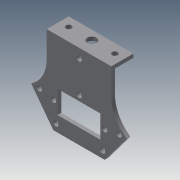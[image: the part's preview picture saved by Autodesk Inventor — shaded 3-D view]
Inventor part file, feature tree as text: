
AUTODESK INVENTOR PART (.ipt)
format: ipt  version: 2015 (Build 190159000, 159)  size: 1,127,936 bytes
history: native  units: mm
features: sketch x103, extrude x90, fillet x2
ambient origin geometry x8: Origin, YZ Plane, XZ Plane, XY Plane, X Axis, Y Axis, Z Axis, Center Point
bodies: Solid1 (feature_tree)
feature tree (195):
  extrude  "Extrusion1"  Depth=10.0mm
  extrude  "Extrusion2"  Depth=10.0mm
  sketch  "Sketch3"  dims[d8=2.0mm d9=0.0mm d11=3.0mm]
  extrude  "Extrusion3"  Depth=2.0mm
  extrude  "Extrusion4"  Depth=3.0mm
  extrude  "Extrusion5"  Depth=10.0mm TaperAngle=0.0deg
  extrude  "Extrusion6"  Depth=3.0mm
  sketch  "Sketch8"  dims[d24=10.0mm d25=0.0mm d26=2.0mm d27=0.0mm]
  extrude  "Extrusion7"  Depth=3.0mm
  extrude  "Extrusion8"  Depth=2.0mm TaperAngle=0.0deg
  extrude  "Extrusion9"  Depth=3.0mm
  extrude  "Extrusion10"  Depth=2.0mm TaperAngle=0.0deg
  extrude  "Extrusion11"  Depth=2.0mm
  extrude  "Extrusion12"  Depth=12.0mm
  extrude  "Extrusion13"  Depth=2.0mm
  sketch  "Sketch16"  dims[d61=4.0mm d62=4.0mm]
  extrude  "Extrusion14"  Depth=2.0mm
  extrude  "Extrusion15"  Depth=12.0mm
  extrude  "Extrusion16"  Depth=4.0mm
  extrude  "Extrusion17"  Depth=2.0mm
  sketch  "Sketch21"  dims[d75=30.0mm d77=2.0mm d78=0.0mm]
  extrude  "Extrusion18"  Depth=12.0mm
  extrude  "Extrusion19"  Depth=2.0mm
  extrude  "Extrusion20"  Depth=20.0mm
  extrude  "Extrusion21"  Depth=2.0mm TaperAngle=0.0deg
  extrude  "Extrusion22"  Depth=2.3mm
  extrude  "Extrusion23"  Depth=2.0mm
  extrude  "Extrusion24"  Depth=2.0mm TaperAngle=0.0deg
  extrude  "Extrusion25"  Depth=3.0mm
  extrude  "Extrusion26"  Depth=2.0mm TaperAngle=0.0deg
  extrude  "Extrusion27"  Depth=2.0mm TaperAngle=0.0deg
  extrude  "Extrusion28"  Depth=4.0mm
  extrude  "Extrusion29"  Depth=3.0mm
  extrude  "Extrusion30"  Depth=3.0mm
  extrude  "Extrusion31"  Depth=3.0mm
  extrude  "Extrusion32"  Depth=4.0mm
  extrude  "Extrusion33"  Depth=3.0mm
  extrude  "Extrusion34"  Depth=2.0mm TaperAngle=0.0deg
  extrude  "Extrusion35"  Depth=2.3mm
  extrude  "Extrusion36"  Depth=4.0mm
  extrude  "Extrusion37"  Depth=2.0mm
  sketch  "Sketch42"  dims[d147=24.0mm d148=24.0mm]
  sketch  "Sketch43"  dims[d149=2.0mm d150=0.0mm d151=2.0mm d152=0.0mm]
  extrude  "Extrusion38"  Depth=2.0mm TaperAngle=0.0deg
  extrude  "Extrusion39"  Depth=2.0mm TaperAngle=0.0deg
  extrude  "Extrusion40"  Depth=20.0mm
  extrude  "Extrusion41"  Depth=20.0mm
  extrude  "Extrusion42"  Depth=24.0mm
  extrude  "Extrusion43"  Depth=2.0mm TaperAngle=0.0deg
  extrude  "Extrusion44"  Depth=3.0mm
  extrude  "Extrusion45"  Depth=20.0mm
  extrude  "Extrusion46"  Depth=2.0mm TaperAngle=0.0deg
  extrude  "Extrusion47"  Depth=2.0mm
  extrude  "Extrusion48"  Depth=3.0mm
  fillet  "Fillet1"  Radius=3.0mm
  extrude  "Extrusion49"  Depth=2.5mm
  fillet  "Fillet2"  Radius=2.0mm
  extrude  "Extrusion50"  Depth=2.0mm
  extrude  "Extrusion51"  Depth=2.5mm
  extrude  "Extrusion52"  Depth=20.0mm
  extrude  "Extrusion53"  Depth=20.0mm
  extrude  "Extrusion54"  Depth=2.0mm TaperAngle=0.0deg
  extrude  "Extrusion55"  Depth=1.5mm
  extrude  "Extrusion56"  Depth=20.0mm
  extrude  "Extrusion57"  Depth=20.0mm
  extrude  "Extrusion58"  Depth=24.0mm
  extrude  "Extrusion59"  Depth=2.0mm
  extrude  "Extrusion60"  Depth=3.0mm
  extrude  "Extrusion61"  Depth=3.0mm
  extrude  "Extrusion62"  Depth=2.0mm TaperAngle=0.0deg
  sketch  "Sketch67"  dims[d218=3.0mm d219=3.0mm]
  extrude  "Extrusion63"  Depth=2.0mm
  extrude  "Extrusion64"  Depth=2.0mm TaperAngle=0.0deg
  extrude  "Extrusion65"  Depth=14.4mm
  sketch  "Sketch71"  dims[d228=1.5mm d229=3.0mm]
  sketch  "Sketch72"  dims[d230=2.0mm d231=0.0mm d233=2.0mm d234=0.0mm]
  extrude  "Extrusion66"  Depth=1.5mm
  sketch  "Sketch73"  dims[d236=14.5mm d237=13.95mm]
  sketch  "Sketch74"  dims[d238=13.95mm d239=3.0mm]
  extrude  "Extrusion67"  Depth=3.0mm
  extrude  "Extrusion68"  Depth=2.0mm TaperAngle=0.0deg
  extrude  "Extrusion69"  Depth=1.5mm
  extrude  "Extrusion70"  Depth=14.4mm
  extrude  "Extrusion71"  Depth=1.5mm
  sketch  "Sketch80"  dims[d256=19.0mm d259=19.0mm]
  sketch  "Sketch81"  dims[d260=2.0mm d261=0.0mm d262=10.0mm]
  extrude  "Extrusion72"  Depth=2.0mm TaperAngle=0.0deg
  extrude  "Extrusion73"  Depth=13.95mm
  sketch  "Sketch84"  dims[d269=2.0mm d270=0.0mm d271=2.0mm d272=0.0mm]
  extrude  "Extrusion74"  Depth=3.0mm
  extrude  "Extrusion75"  Depth=2.0mm TaperAngle=0.0deg
  extrude  "Extrusion76"  Depth=2.0mm
  extrude  "Extrusion77"  Depth=2.0mm
  extrude  "Extrusion78"  Depth=2.0mm
  extrude  "Extrusion79"  Depth=2.0mm TaperAngle=0.0deg
  extrude  "Extrusion80"  Depth=19.0mm
  extrude  "Extrusion81"  Depth=10.0mm
  extrude  "Extrusion82"  Depth=4.0mm
  extrude  "Extrusion83"  Depth=2.0mm TaperAngle=0.0deg
  sketch  "Sketch95"  dims[d298=10.0mm d299=0.0mm]
  extrude  "Extrusion84"  Depth=2.0mm TaperAngle=0.0deg
  extrude  "Extrusion85"  Depth=2.0mm TaperAngle=0.0deg
  extrude  "Extrusion86"  Depth=10.0mm TaperAngle=0.0deg
  extrude  "Extrusion87"  Depth=2.0mm TaperAngle=0.0deg
  sketch  "Sketch100"  dims[d310=16.0mm]
  extrude  "Extrusion88"  Depth=1.5mm TaperAngle=0.0deg
  extrude  "Extrusion89"  Depth=1.5mm
  extrude  "Extrusion90"  Depth=16.0mm
  sketch  "Sketch1"  dims[d2=10.0mm d3=10.0mm]
  sketch  "Sketch2"  dims[d4=10.0mm d7=10.0mm]
  sketch  "Sketch4"  dims[d12=3.0mm d14=3.0mm]
  sketch  "Sketch5"  dims[d15=3.0mm d16=10.0mm d17=0.0mm]
  sketch  "Sketch6"  dims[d20=6.0mm d21=3.0mm]
  sketch  "Sketch7"  dims[d22=6.0mm d23=3.0mm]
  sketch  "Sketch9"  dims[d34=3.0mm d36=3.0mm]
  sketch  "Sketch10"  dims[d37=2.0mm d38=0.0mm d39=2.0mm d40=0.0mm]
  sketch  "Sketch11"  dims[d48=2.0mm d49=4.0mm]
  sketch  "Sketch12"  dims[d51=12.0mm d52=4.0mm]
  sketch  "Sketch13"  dims[d53=2.0mm d54=0.0mm d55=1.8mm]
  sketch  "Sketch14"  dims[d56=2.0mm d57=4.0mm]
  sketch  "Sketch15"  dims[d58=2.0mm d59=0.0mm d60=12.0mm]
  sketch  "Sketch17"  dims[d63=2.0mm d64=0.0mm d65=16.0mm]
  sketch  "Sketch18"  dims[d66=12.0mm d67=10.4mm]
  sketch  "Sketch19"  dims[d68=2.0mm d69=0.0mm d70=4.0mm]
  sketch  "Sketch20"  dims[d71=2.0mm d72=0.0mm d74=20.0mm]
  sketch  "Sketch22"  dims[d83=2.3mm d84=2.3mm]
  sketch  "Sketch23"  dims[d85=2.0mm d86=0.0mm d90=24.0mm]
  sketch  "Sketch24"  dims[d92=24.0mm d93=2.0mm d94=0.0mm]
  sketch  "Sketch25"  dims[d97=3.0mm d98=3.0mm]
  sketch  "Sketch26"  dims[d100=3.0mm d101=2.0mm d102=0.0mm]
  sketch  "Sketch27"  dims[d103=2.0mm d104=0.0mm d105=2.0mm d106=0.0mm]
  sketch  "Sketch28"  dims[d111=4.0mm d112=4.0mm]
  sketch  "Sketch29"  dims[d113=3.0mm d114=3.0mm]
  sketch  "Sketch30"  dims[d116=3.0mm d117=3.0mm]
  sketch  "Sketch31"  dims[d118=3.0mm d119=3.0mm]
  sketch  "Sketch32"  dims[d120=3.0mm d121=4.0mm]
  sketch  "Sketch33"  dims[d122=3.0mm d123=3.0mm]
  sketch  "Sketch34"  dims[d124=3.0mm d125=2.0mm d126=0.0mm]
  sketch  "Sketch35"  dims[d127=2.3mm d128=2.3mm]
  sketch  "Sketch36"  dims[d131=4.0mm d132=4.0mm]
  sketch  "Sketch37"  dims[d133=2.0mm d134=0.0mm d135=2.3mm]
  sketch  "Sketch38"  dims[d136=2.3mm d137=2.0mm d138=0.0mm]
  sketch  "Sketch39"  dims[d139=3.0mm d140=2.0mm d141=0.0mm]
  sketch  "Sketch40"  dims[d142=2.0mm d143=0.0mm d144=20.0mm]
  sketch  "Sketch41"  dims[d145=14.0mm d146=20.0mm]
  sketch  "Sketch44"  dims[d157=3.0mm d158=3.0mm]
  sketch  "Sketch45"  dims[d159=2.0mm d160=0.0mm d161=20.0mm]
  sketch  "Sketch46"  dims[d162=20.0mm d163=2.0mm d164=0.0mm]
  sketch  "Sketch47"  dims[d165=2.0mm d166=0.0mm d167=3.0mm]
  sketch  "Sketch48"  dims[d168=3.0mm d169=3.0mm d170=3.0mm]
  sketch  "Sketch49"  dims[d171=2.5mm d172=2.5mm d173=2.0mm d174=0.0mm]
  sketch  "Sketch50"  dims[d175=2.0mm d176=0.0mm d178=12.5mm]
  sketch  "Sketch51"  dims[d179=12.5mm d180=2.5mm]
  sketch  "Sketch52"  dims[d181=2.5mm d183=20.0mm]
  sketch  "Sketch53"  dims[d185=20.0mm d186=25.0mm]
  sketch  "Sketch54"  dims[d187=25.0mm d188=2.0mm d189=0.0mm]
  sketch  "Sketch55"  dims[d190=1.5mm d191=1.5mm]
  sketch  "Sketch56"  dims[d192=1.5mm d193=20.0mm]
  sketch  "Sketch57"  dims[d194=1.5mm d195=20.0mm]
  sketch  "Sketch58"  dims[d196=24.0mm d197=24.0mm]
  sketch  "Sketch59"  dims[d198=2.0mm d199=0.0mm d200=3.4mm]
  sketch  "Sketch60"  dims[d201=3.4mm d202=3.0mm]
  sketch  "Sketch61"  dims[d203=3.0mm d204=3.0mm]
  sketch  "Sketch62"  dims[d205=3.0mm d206=2.0mm d207=0.0mm]
  sketch  "Sketch63"  dims[d208=2.0mm d209=0.0mm d210=17.0mm]
  sketch  "Sketch64"  dims[d211=14.4mm d212=2.0mm d213=0.0mm]
  sketch  "Sketch65"  dims[d214=19.5mm d215=14.4mm]
  sketch  "Sketch66"  dims[d216=1.5mm d217=1.5mm]
  sketch  "Sketch68"  dims[d220=2.0mm d221=0.0mm d222=2.0mm d223=0.0mm]
  sketch  "Sketch69"  dims[d224=19.5mm d225=1.5mm]
  sketch  "Sketch70"  dims[d226=3.0mm d227=14.4mm]
  sketch  "Sketch75"  dims[d241=3.0mm d242=2.0mm d243=0.0mm]
  sketch  "Sketch76"  dims[d244=2.0mm d245=0.0mm d248=14.4mm]
  sketch  "Sketch77"  dims[d249=21.6mm d250=2.0mm]
  sketch  "Sketch78"  dims[d251=2.0mm d252=4.0mm]
  sketch  "Sketch79"  dims[d253=4.0mm d254=2.0mm d255=0.0mm]
  sketch  "Sketch82"  dims[d263=4.0mm d264=4.0mm]
  sketch  "Sketch83"  dims[d265=2.0mm d266=0.0mm d267=2.0mm d268=0.0mm]
  sketch  "Sketch85"  dims[d273=3.6mm d274=2.0mm d275=0.0mm]
  sketch  "Sketch86"  dims[d276=1.5mm d277=10.0mm d278=0.0mm]
  sketch  "Sketch87"  dims[d279=2.0mm d280=0.5mm d281=0.0mm]
  sketch  "Sketch88"  dims[d282=0.5mm d283=1.5mm d284=0.0mm]
  sketch  "Sketch89"  dims[d285=1.5mm d286=0.0mm d287=10.4mm]
  sketch  "Sketch90"  dims[d288=14.398895mm d289=16.0mm]
  sketch  "Sketch91"  dims[d290=1.5mm d291=0.0mm]
  sketch  "Sketch92"  dims[d292=1.5mm d293=0.0mm]
  sketch  "Sketch93"  dims[d294=10.0mm d295=0.0mm]
  sketch  "Sketch94"  dims[d296=10.0mm d297=0.0mm]
  sketch  "Sketch96"  dims[d300=20.0mm d301=0.0mm]
  sketch  "Sketch97"  dims[d306=1.5mm d307=0.0mm]
  sketch  "Sketch98"  dims[d308=4.0mm]
  sketch  "Sketch99"  dims[d309=7.0mm]
  sketch  "Sketch101"  dims[d311=3.0mm]
  sketch  "Sketch102"  dims[d312=7.0mm]
  sketch  "Sketch103"  dims[d313=16.0mm d314=1.5mm d315=0.0mm d316=5.0mm d317=1.5mm d318=0.0mm d319=1.5mm d320=10.0mm d321=0.0mm d322=7.0mm d323=7.0mm d324=4.0mm d325=7.0mm d326=4.0mm d327=7.0mm d328=4.0mm d329=1.5mm d330=0.0mm d331=4.0mm d332=4.129mm d333=7.0mm d335=3.072mm d336=7.0mm d337=15.0mm d338=1.5mm d339=0.0mm d341=1.5mm d342=0.0mm d343=0.5mm d344=7.0mm d345=18.0mm d346=7.0mm d347=1.5mm d348=0.0mm d349=7.0mm d351=7.0mm d353=1.5mm d354=0.0mm d359=8.3mm d360=11.6mm d361=23.6mm d362=12.4mm d363=1.5mm d364=0.0mm d365=27.9mm d366=0.4mm d367=1.5mm d368=0.0mm d370=0.3mm d371=0.3mm d372=1.5mm d373=0.0mm d374=5.0mm d375=5.0mm d376=1.5mm d377=0.0mm d378=6.3mm d379=12.6mm d380=3.0mm d381=3.0mm d382=1.5mm d383=0.0mm d391=1.5mm d392=0.0mm d395=7.0mm d396=19.0mm d399=7.0mm d400=1.5mm d401=0.0mm d403=1.5mm d404=0.0mm d406=1.5mm d407=3.0mm d409=1.5mm d410=3.0mm d411=1.5mm d412=0.0mm d413=14.5mm d414=3.0mm d415=1.5mm d416=0.0mm d417=3.0mm d418=1.5mm d419=3.0mm d420=2.0mm d421=3.0mm d422=3.0mm d423=1.5mm d424=0.0mm d425=1.5mm d426=1.5mm d427=0.0mm d428=1.5mm d429=1.5mm d430=0.0mm d431=1.5mm d432=0.0mm d433=3.0mm d434=3.0mm d435=3.0mm d436=3.0mm d437=1.5mm d438=0.0mm d439=1.5mm d440=0.0mm d441=3.0mm d442=3.0mm d443=1.5mm d444=0.0mm d445=0.5mm d446=0.0mm d447=0.5mm d448=0.0mm d449=5.0mm d450=5.0mm d451=3.0mm d452=3.0mm d453=2.0mm d454=0.0mm d455=2.0mm d456=2.0mm d457=2.0mm d458=0.0mm d459=2.0mm d460=0.0mm d461=2.0mm d462=0.0mm d464=3.0mm d465=3.0mm d466=2.0mm d467=0.0mm]
